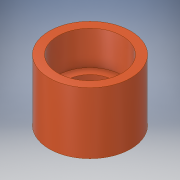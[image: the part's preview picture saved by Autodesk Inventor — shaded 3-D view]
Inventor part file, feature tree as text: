
AUTODESK INVENTOR PART (.ipt)
format: ipt  version: 2017 (Build 210142000, 142)  size: 140,288 bytes
history: native  units: in
note: dims shown in document units (in); Inventor stores cm internally (conversion verified against a paired STEP export)
features: revolve x1, sketch x1
ambient origin geometry x8: Origin, YZ Plane, XZ Plane, XY Plane, X Axis, Y Axis, Z Axis, Center Point
bodies: Body1 (feature_tree)
feature tree (2):
  revolve  "Revolution3"  [1 undecoded]
  sketch  "Sketch1"  dims[d0=0.25in d1=0.1718in d2=15.0deg d4=0.25in d5=1.5in d6=1.25in d7=0.25in d11=0.25in d13=0.5in d15=0.25in d16=0.25in d18=0.125in d19=0.5in d20=0.125in d21=0.25in d22=0.125in d23=0.125in d24=0.25in d25=0.5in d26=2.292in d27=0.5in d29=0.5in d31=90.0deg]
note: 1 required parameter value undecoded (feature->parameter linkage not recoverable at this tier; creation-order binding heuristic only, values carry confidence <= 0.55)
